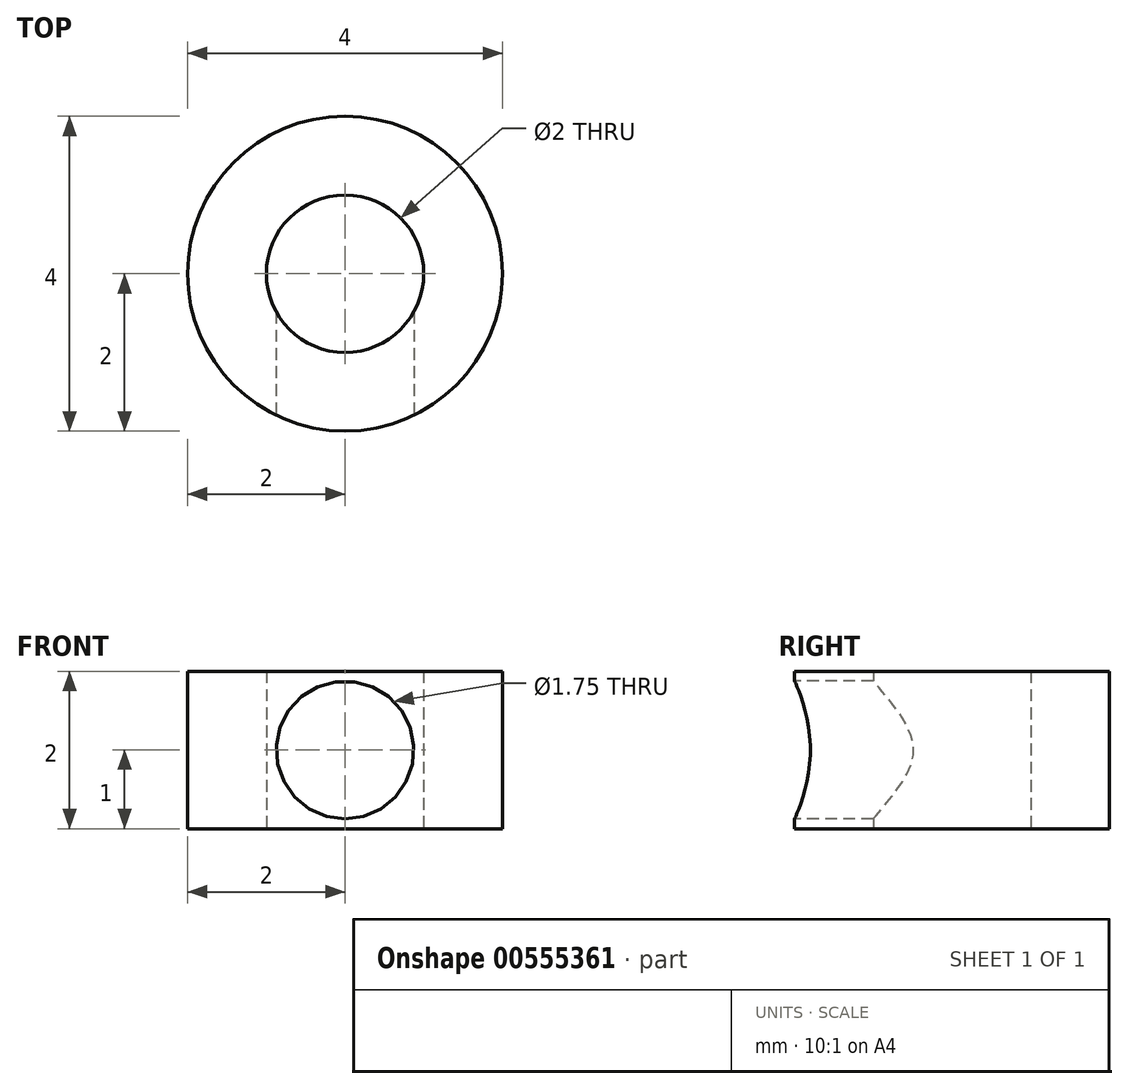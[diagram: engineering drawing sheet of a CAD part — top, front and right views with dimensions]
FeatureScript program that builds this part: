
annotation { "Feature Type Name" : "Feature", "Feature Type Description" : "" }
export const myFeature = defineFeature(function(context is Context, id is Id, definition is map)
    precondition{}
    {
        {
            var Q0;
            Q0=qCreatedBy(makeId("Top.planeOp"),FACE);
            var sketch = newSketch(context, id + "F0", { "sketchPlane" : qUnion([Q0])});
            skCircle(sketch, "E0", {"center": v(0, 0) * mm, "radius": 1 * mm});
            skCircle(sketch, "E1", {"center": v(0, 0) * mm, "radius": 2 * mm});
            skLineSegment(sketch, "E2", {"start": v(0, 0) * mm, "end": v(0, -2) * mm, "construction": true});
            skPoint(sketch, "E3", {"position": v(0, -2) * mm});
            skSolve(sketch);
        }
        {
            var Q0;
            Q0=makeQuery(id+"F0.imprint","IMPRINT",FACE,{"disambiguationData":[TD([[makeQuery(id+"F0.imprint","IMPRINT",EDGE,{"derivedFrom":sQuery(id+"F0.wireOp",EDGE,"E0")}),-1.0]])]});
            extrude(context, id + "F1", {"entities" : qUnion([Q0]), "depth" : 2 * mm, "offsetDistance" : 25 * mm});
        }
        {
            var Q0;
            Q0=qCreatedBy(makeId("Front.planeOp"),FACE);
            var Q1;
            Q1=sQuery(id+"F0.wireOp",VERTEX,"E3");
            cPlane(context, id + "F2", {"entities" : qUnion([Q0, Q1]), "cplaneType" : CPlaneType.PLANE_POINT, "offset" : 25 * mm, "width" : 150 * mm, "height" : 150 * mm});
        }
        {
            var Q0;
            Q0=qCreatedBy(id+"F2.planeOp",FACE);
            var sketch = newSketch(context, id + "F3", { "sketchPlane" : qUnion([Q0])});
            skPoint(sketch, "E4", {"position": v(0, 0) * mm});
            skLineSegment(sketch, "E5", {"start": v(0, 0) * mm, "end": v(0, 2) * mm, "construction": true});
            skPoint(sketch, "E6", {"position": v(0, 1) * mm});
            skSolve(sketch);
        }
        {
            var Q0;
            Q0=sQuery(id+"F3.wireOp",VERTEX,"E6");
            var Q1;
            Q1=makeQuery(id+"F1.opExtrude","SWEPT_BODY",BODY,{"disambiguationData":[OSD([sQuery(id+"F0.wireOp",EDGE,"E0"),sQuery(id+"F0.wireOp",EDGE,"E1")])]});
            hole(context, id + "F4", {"style" : HoleStyle.SIMPLE, "endStyle" : HoleEndStyle.BLIND, "standardTappedOrClearance" : lookupTablePath({ "standard" : "ISO", "engagement" : "75%", "pitch" : "0.25 mm", "size" : "M2", "type" : "Tapped" }), "standardBlindInLast" : lookupTablePath({ "standard" : "ISO", "fit" : "Normal", "engagement" : "75%", "pitch" : "0.25 mm", "size" : "M2", "type" : "Clearance & tapped" }), "holeDiameter" : 1.75 * mm, "majorDiameter" : 2 * mm, "showTappedDepth" : true, "holeDepth" : 1.75 * mm, "isTappedThrough" : true, "tappedDepth" : 1 * mm, "tapClearance" : 3, "locations" : qUnion([Q0]), "scope" : qUnion([Q1])});
        }
    });
